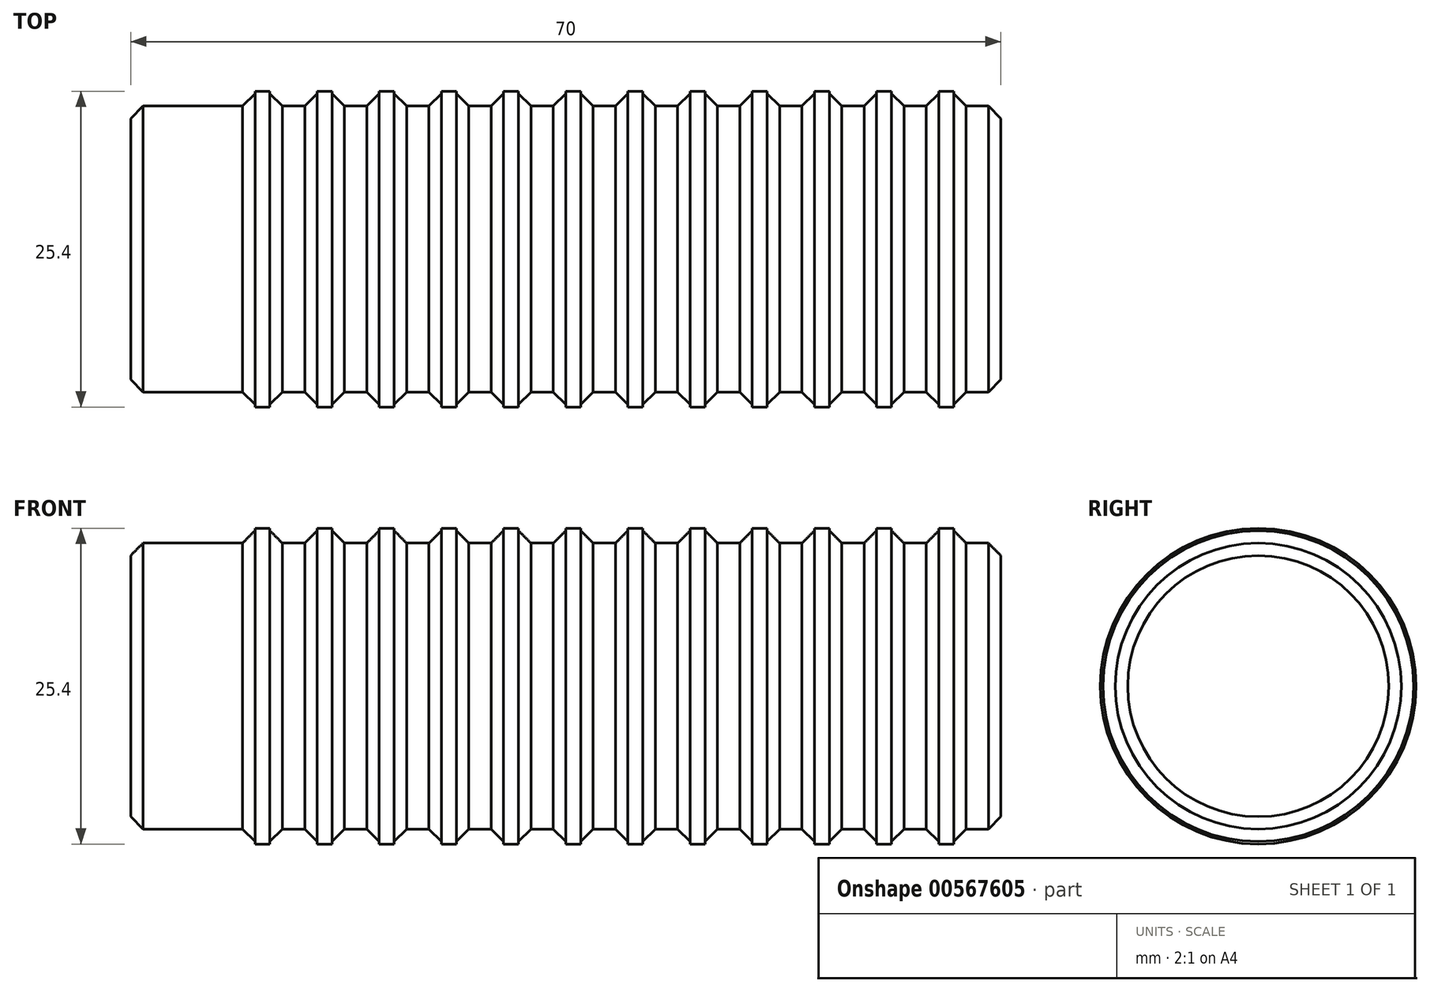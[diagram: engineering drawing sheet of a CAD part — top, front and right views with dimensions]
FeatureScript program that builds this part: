
annotation { "Feature Type Name" : "Feature", "Feature Type Description" : "" }
export const myFeature = defineFeature(function(context is Context, id is Id, definition is map)
    precondition{}
    {
        {
            var Q0;
            Q0=qCreatedBy(makeId("Top.planeOp"),FACE);
            var sketch = newSketch(context, id + "F0", { "sketchPlane" : qUnion([Q0])});
            skLineSegment(sketch, "E0.bottom", {"start": v(-26.21, 0) * mm, "end": v(43.79, 0) * mm});
            skLineSegment(sketch, "E0.top", {"start": v(-26.21, 11.5) * mm, "end": v(43.79, 11.5) * mm});
            skLineSegment(sketch, "E0.left", {"start": v(-26.21, 0) * mm, "end": v(-26.21, 11.5) * mm});
            skLineSegment(sketch, "E0.right", {"start": v(43.79, 0) * mm, "end": v(43.79, 11.5) * mm});
            skLineSegment(sketch, "E1.bottom", {"start": v(-21.21, 11.5) * mm, "end": v(-20.01, 11.5) * mm});
            skLineSegment(sketch, "E1.top", {"start": v(-21.21, 12.7) * mm, "end": v(-20.01, 12.7) * mm});
            skLineSegment(sketch, "E1.left", {"start": v(-21.21, 11.5) * mm, "end": v(-21.21, 12.7) * mm});
            skLineSegment(sketch, "E1.right", {"start": v(-20.01, 11.5) * mm, "end": v(-20.01, 12.7) * mm});
            skLineSegment(sketch, "E2.1.0.0", {"start": v(-15.01, 11.5) * mm, "end": v(-15.01, 12.7) * mm});
            skLineSegment(sketch, "E2.1.0.1", {"start": v(-16.21, 11.5) * mm, "end": v(-16.21, 12.7) * mm});
            skLineSegment(sketch, "E2.1.0.2", {"start": v(-16.21, 12.7) * mm, "end": v(-15.01, 12.7) * mm});
            skLineSegment(sketch, "E2.1.0.3", {"start": v(-16.21, 11.5) * mm, "end": v(-15.01, 11.5) * mm});
            skLineSegment(sketch, "E2.2.0.0", {"start": v(-10.01, 11.5) * mm, "end": v(-10.01, 12.7) * mm});
            skLineSegment(sketch, "E2.2.0.1", {"start": v(-11.21, 11.5) * mm, "end": v(-11.21, 12.7) * mm});
            skLineSegment(sketch, "E2.2.0.2", {"start": v(-11.21, 12.7) * mm, "end": v(-10.01, 12.7) * mm});
            skLineSegment(sketch, "E2.2.0.3", {"start": v(-11.21, 11.5) * mm, "end": v(-10.01, 11.5) * mm});
            skLineSegment(sketch, "E2.3.0.0", {"start": v(-5.01, 11.5) * mm, "end": v(-5.01, 12.7) * mm});
            skLineSegment(sketch, "E2.3.0.1", {"start": v(-6.21, 11.5) * mm, "end": v(-6.21, 12.7) * mm});
            skLineSegment(sketch, "E2.3.0.2", {"start": v(-6.21, 12.7) * mm, "end": v(-5.01, 12.7) * mm});
            skLineSegment(sketch, "E2.3.0.3", {"start": v(-6.21, 11.5) * mm, "end": v(-5.01, 11.5) * mm});
            skLineSegment(sketch, "E2.4.0.0", {"start": v(-0.01, 11.5) * mm, "end": v(-0.01, 12.7) * mm});
            skLineSegment(sketch, "E2.4.0.1", {"start": v(-1.21, 11.5) * mm, "end": v(-1.21, 12.7) * mm});
            skLineSegment(sketch, "E2.4.0.2", {"start": v(-1.21, 12.7) * mm, "end": v(-0.01, 12.7) * mm});
            skLineSegment(sketch, "E2.4.0.3", {"start": v(-1.21, 11.5) * mm, "end": v(-0.01, 11.5) * mm});
            skLineSegment(sketch, "E2.direction1", {"start": v(-21.21, 11.5) * mm, "end": v(-16.21, 11.5) * mm, "construction": true});
            skLineSegment(sketch, "E3.0.5.0", {"start": v(4.99, 11.5) * mm, "end": v(4.99, 12.7) * mm});
            skLineSegment(sketch, "E3.3.5.0", {"start": v(3.79, 11.5) * mm, "end": v(3.79, 12.7) * mm});
            skLineSegment(sketch, "E3.6.5.0", {"start": v(3.79, 12.7) * mm, "end": v(4.99, 12.7) * mm});
            skLineSegment(sketch, "E3.9.5.0", {"start": v(3.79, 11.5) * mm, "end": v(4.99, 11.5) * mm});
            skLineSegment(sketch, "E3.0.6.0", {"start": v(9.99, 11.5) * mm, "end": v(9.99, 12.7) * mm});
            skLineSegment(sketch, "E3.3.6.0", {"start": v(8.79, 11.5) * mm, "end": v(8.79, 12.7) * mm});
            skLineSegment(sketch, "E3.6.6.0", {"start": v(8.79, 12.7) * mm, "end": v(9.99, 12.7) * mm});
            skLineSegment(sketch, "E3.9.6.0", {"start": v(8.79, 11.5) * mm, "end": v(9.99, 11.5) * mm});
            skLineSegment(sketch, "E3.0.7.0", {"start": v(14.99, 11.5) * mm, "end": v(14.99, 12.7) * mm});
            skLineSegment(sketch, "E3.3.7.0", {"start": v(13.79, 11.5) * mm, "end": v(13.79, 12.7) * mm});
            skLineSegment(sketch, "E3.6.7.0", {"start": v(13.79, 12.7) * mm, "end": v(14.99, 12.7) * mm});
            skLineSegment(sketch, "E3.9.7.0", {"start": v(13.79, 11.5) * mm, "end": v(14.99, 11.5) * mm});
            skLineSegment(sketch, "E3.0.8.0", {"start": v(19.99, 11.5) * mm, "end": v(19.99, 12.7) * mm});
            skLineSegment(sketch, "E3.3.8.0", {"start": v(18.79, 11.5) * mm, "end": v(18.79, 12.7) * mm});
            skLineSegment(sketch, "E3.6.8.0", {"start": v(18.79, 12.7) * mm, "end": v(19.99, 12.7) * mm});
            skLineSegment(sketch, "E3.9.8.0", {"start": v(18.79, 11.5) * mm, "end": v(19.99, 11.5) * mm});
            skLineSegment(sketch, "E4.0.9.0", {"start": v(24.99, 11.5) * mm, "end": v(24.99, 12.7) * mm});
            skLineSegment(sketch, "E4.3.9.0", {"start": v(23.79, 11.5) * mm, "end": v(23.79, 12.7) * mm});
            skLineSegment(sketch, "E4.6.9.0", {"start": v(23.79, 12.7) * mm, "end": v(24.99, 12.7) * mm});
            skLineSegment(sketch, "E4.9.9.0", {"start": v(23.79, 11.5) * mm, "end": v(24.99, 11.5) * mm});
            skLineSegment(sketch, "E4.0.10.0", {"start": v(29.99, 11.5) * mm, "end": v(29.99, 12.7) * mm});
            skLineSegment(sketch, "E4.3.10.0", {"start": v(28.79, 11.5) * mm, "end": v(28.79, 12.7) * mm});
            skLineSegment(sketch, "E4.6.10.0", {"start": v(28.79, 12.7) * mm, "end": v(29.99, 12.7) * mm});
            skLineSegment(sketch, "E4.9.10.0", {"start": v(28.79, 11.5) * mm, "end": v(29.99, 11.5) * mm});
            skLineSegment(sketch, "E4.0.11.0", {"start": v(34.99, 11.5) * mm, "end": v(34.99, 12.7) * mm});
            skLineSegment(sketch, "E4.3.11.0", {"start": v(33.79, 11.5) * mm, "end": v(33.79, 12.7) * mm});
            skLineSegment(sketch, "E4.6.11.0", {"start": v(33.79, 12.7) * mm, "end": v(34.99, 12.7) * mm});
            skLineSegment(sketch, "E4.9.11.0", {"start": v(33.79, 11.5) * mm, "end": v(34.99, 11.5) * mm});
            skLineSegment(sketch, "E4.0.12.0", {"start": v(39.99, 11.5) * mm, "end": v(39.99, 12.7) * mm});
            skLineSegment(sketch, "E4.3.12.0", {"start": v(38.79, 11.5) * mm, "end": v(38.79, 12.7) * mm});
            skLineSegment(sketch, "E4.6.12.0", {"start": v(38.79, 12.7) * mm, "end": v(39.99, 12.7) * mm});
            skLineSegment(sketch, "E4.9.12.0", {"start": v(38.79, 11.5) * mm, "end": v(39.99, 11.5) * mm});
            skSolve(sketch);
        }
        {
            var Q0;
            Q0=makeQuery(id+"F0.imprint","IMPRINT",FACE,{"disambiguationData":[TD([[makeQuery(id+"F0.imprint","IMPRINT",EDGE,{"derivedFrom":sQuery(id+"F0.wireOp",EDGE,"E0.bottom")}),1.0]])]});
            var Q1;
            Q1=makeQuery(id+"F0.imprint","IMPRINT",FACE,{"disambiguationData":[TD([[makeQuery(id+"F0.imprint","IMPRINT",EDGE,{"derivedFrom":sQuery(id+"F0.wireOp",EDGE,"E3.0.8.0")}),1.0]])]});
            var Q2;
            Q2=makeQuery(id+"F0.imprint","IMPRINT",FACE,{"disambiguationData":[TD([[makeQuery(id+"F0.imprint","IMPRINT",EDGE,{"derivedFrom":sQuery(id+"F0.wireOp",EDGE,"E3.0.7.0")}),1.0]])]});
            var Q3;
            Q3=makeQuery(id+"F0.imprint","IMPRINT",FACE,{"disambiguationData":[TD([[makeQuery(id+"F0.imprint","IMPRINT",EDGE,{"derivedFrom":sQuery(id+"F0.wireOp",EDGE,"E3.0.6.0")}),1.0]])]});
            var Q4;
            Q4=makeQuery(id+"F0.imprint","IMPRINT",FACE,{"disambiguationData":[TD([[makeQuery(id+"F0.imprint","IMPRINT",EDGE,{"derivedFrom":sQuery(id+"F0.wireOp",EDGE,"E3.0.5.0")}),1.0]])]});
            var Q5;
            Q5=makeQuery(id+"F0.imprint","IMPRINT",FACE,{"disambiguationData":[TD([[makeQuery(id+"F0.imprint","IMPRINT",EDGE,{"derivedFrom":sQuery(id+"F0.wireOp",EDGE,"E2.4.0.0")}),1.0]])]});
            var Q6;
            Q6=makeQuery(id+"F0.imprint","IMPRINT",FACE,{"disambiguationData":[TD([[makeQuery(id+"F0.imprint","IMPRINT",EDGE,{"derivedFrom":sQuery(id+"F0.wireOp",EDGE,"E2.3.0.0")}),1.0]])]});
            var Q7;
            Q7=makeQuery(id+"F0.imprint","IMPRINT",FACE,{"disambiguationData":[TD([[makeQuery(id+"F0.imprint","IMPRINT",EDGE,{"derivedFrom":sQuery(id+"F0.wireOp",EDGE,"E2.2.0.0")}),1.0]])]});
            var Q8;
            Q8=makeQuery(id+"F0.imprint","IMPRINT",FACE,{"disambiguationData":[TD([[makeQuery(id+"F0.imprint","IMPRINT",EDGE,{"derivedFrom":sQuery(id+"F0.wireOp",EDGE,"E2.1.0.0")}),1.0]])]});
            var Q9;
            Q9=makeQuery(id+"F0.imprint","IMPRINT",FACE,{"disambiguationData":[TD([[makeQuery(id+"F0.imprint","IMPRINT",EDGE,{"derivedFrom":sQuery(id+"F0.wireOp",EDGE,"E1.bottom")}),1.0]])]});
            var Q10;
            Q10=makeQuery(id+"F0.imprint","IMPRINT",FACE,{"disambiguationData":[TD([[makeQuery(id+"F0.imprint","IMPRINT",EDGE,{"derivedFrom":sQuery(id+"F0.wireOp",EDGE,"E4.0.9.0")}),1.0]])]});
            var Q11;
            Q11=makeQuery(id+"F0.imprint","IMPRINT",FACE,{"disambiguationData":[TD([[makeQuery(id+"F0.imprint","IMPRINT",EDGE,{"derivedFrom":sQuery(id+"F0.wireOp",EDGE,"E4.0.10.0")}),1.0]])]});
            var Q12;
            Q12=makeQuery(id+"F0.imprint","IMPRINT",FACE,{"disambiguationData":[TD([[makeQuery(id+"F0.imprint","IMPRINT",EDGE,{"derivedFrom":sQuery(id+"F0.wireOp",EDGE,"E4.0.11.0")}),1.0]])]});
            var Q13;
            Q13=makeQuery(id+"F0.imprint","IMPRINT",FACE,{"disambiguationData":[TD([[makeQuery(id+"F0.imprint","IMPRINT",EDGE,{"derivedFrom":sQuery(id+"F0.wireOp",EDGE,"E4.0.12.0")}),1.0]])]});
            var Q14;
            Q14=sQuery(id+"F0.wireOp",EDGE,"E0.bottom");
            revolve(context, id + "F1", {"entities" : qUnion([Q0, Q1, Q2, Q3, Q4, Q5, Q6, Q7, Q8, Q9, Q10, Q11, Q12, Q13]), "axis" : qUnion([Q14]), "revolveType" : RevolveType.FULL});
        }
        {
            var Q0;
            Q0=makeQuery(id+"F1.opRevolve","SWEPT_EDGE",EDGE,{"disambiguationData":[OSD([sQuery(id+"F0.wireOp",EDGE,"E0.top"),sQuery(id+"F0.wireOp",EDGE,"E1.bottom"),sQuery(id+"F0.wireOp",EDGE,"E1.left")])]});
            var Q1;
            Q1=makeQuery(id+"F1.opRevolve","SWEPT_EDGE",EDGE,{"disambiguationData":[OSD([sQuery(id+"F0.wireOp",EDGE,"E0.top"),sQuery(id+"F0.wireOp",EDGE,"E2.1.0.1"),sQuery(id+"F0.wireOp",EDGE,"E2.1.0.3")])]});
            var Q2;
            Q2=makeQuery(id+"F1.opRevolve","SWEPT_EDGE",EDGE,{"disambiguationData":[OSD([sQuery(id+"F0.wireOp",EDGE,"E0.top"),sQuery(id+"F0.wireOp",EDGE,"E2.2.0.1"),sQuery(id+"F0.wireOp",EDGE,"E2.2.0.3")])]});
            var Q3;
            Q3=makeQuery(id+"F1.opRevolve","SWEPT_EDGE",EDGE,{"disambiguationData":[OSD([sQuery(id+"F0.wireOp",EDGE,"E0.top"),sQuery(id+"F0.wireOp",EDGE,"E2.3.0.1"),sQuery(id+"F0.wireOp",EDGE,"E2.3.0.3")])]});
            var Q4;
            Q4=makeQuery(id+"F1.opRevolve","SWEPT_EDGE",EDGE,{"disambiguationData":[OSD([sQuery(id+"F0.wireOp",EDGE,"E0.top"),sQuery(id+"F0.wireOp",EDGE,"E3.0.8.0"),sQuery(id+"F0.wireOp",EDGE,"E3.9.8.0")])]});
            var Q5;
            Q5=makeQuery(id+"F1.opRevolve","SWEPT_EDGE",EDGE,{"disambiguationData":[OSD([sQuery(id+"F0.wireOp",EDGE,"E0.top"),sQuery(id+"F0.wireOp",EDGE,"E3.0.7.0"),sQuery(id+"F0.wireOp",EDGE,"E3.9.7.0")])]});
            var Q6;
            Q6=makeQuery(id+"F1.opRevolve","SWEPT_EDGE",EDGE,{"disambiguationData":[OSD([sQuery(id+"F0.wireOp",EDGE,"E0.top"),sQuery(id+"F0.wireOp",EDGE,"E3.0.6.0"),sQuery(id+"F0.wireOp",EDGE,"E3.9.6.0")])]});
            var Q7;
            Q7=makeQuery(id+"F1.opRevolve","SWEPT_EDGE",EDGE,{"disambiguationData":[OSD([sQuery(id+"F0.wireOp",EDGE,"E0.top"),sQuery(id+"F0.wireOp",EDGE,"E3.0.5.0"),sQuery(id+"F0.wireOp",EDGE,"E3.9.5.0")])]});
            var Q8;
            Q8=makeQuery(id+"F1.opRevolve","SWEPT_EDGE",EDGE,{"disambiguationData":[OSD([sQuery(id+"F0.wireOp",EDGE,"E0.top"),sQuery(id+"F0.wireOp",EDGE,"E2.4.0.1"),sQuery(id+"F0.wireOp",EDGE,"E2.4.0.3")])]});
            var Q9;
            Q9=makeQuery(id+"F1.opRevolve","SWEPT_EDGE",EDGE,{"disambiguationData":[OSD([sQuery(id+"F0.wireOp",EDGE,"E0.top"),sQuery(id+"F0.wireOp",EDGE,"E2.4.0.0"),sQuery(id+"F0.wireOp",EDGE,"E2.4.0.3")])]});
            var Q10;
            Q10=makeQuery(id+"F1.opRevolve","SWEPT_EDGE",EDGE,{"disambiguationData":[OSD([sQuery(id+"F0.wireOp",EDGE,"E0.top"),sQuery(id+"F0.wireOp",EDGE,"E1.bottom"),sQuery(id+"F0.wireOp",EDGE,"E1.right")])]});
            var Q11;
            Q11=makeQuery(id+"F1.opRevolve","SWEPT_EDGE",EDGE,{"disambiguationData":[OSD([sQuery(id+"F0.wireOp",EDGE,"E0.top"),sQuery(id+"F0.wireOp",EDGE,"E2.1.0.0"),sQuery(id+"F0.wireOp",EDGE,"E2.1.0.3")])]});
            var Q12;
            Q12=makeQuery(id+"F1.opRevolve","SWEPT_EDGE",EDGE,{"disambiguationData":[OSD([sQuery(id+"F0.wireOp",EDGE,"E0.top"),sQuery(id+"F0.wireOp",EDGE,"E2.2.0.0"),sQuery(id+"F0.wireOp",EDGE,"E2.2.0.3")])]});
            var Q13;
            Q13=makeQuery(id+"F1.opRevolve","SWEPT_EDGE",EDGE,{"disambiguationData":[OSD([sQuery(id+"F0.wireOp",EDGE,"E0.top"),sQuery(id+"F0.wireOp",EDGE,"E2.3.0.0"),sQuery(id+"F0.wireOp",EDGE,"E2.3.0.3")])]});
            var Q14;
            Q14=makeQuery(id+"F1.opRevolve","SWEPT_EDGE",EDGE,{"disambiguationData":[OSD([sQuery(id+"F0.wireOp",EDGE,"E0.top"),sQuery(id+"F0.wireOp",EDGE,"E3.3.5.0"),sQuery(id+"F0.wireOp",EDGE,"E3.9.5.0")])]});
            var Q15;
            Q15=makeQuery(id+"F1.opRevolve","SWEPT_EDGE",EDGE,{"disambiguationData":[OSD([sQuery(id+"F0.wireOp",EDGE,"E0.top"),sQuery(id+"F0.wireOp",EDGE,"E3.3.6.0"),sQuery(id+"F0.wireOp",EDGE,"E3.9.6.0")])]});
            var Q16;
            Q16=makeQuery(id+"F1.opRevolve","SWEPT_EDGE",EDGE,{"disambiguationData":[OSD([sQuery(id+"F0.wireOp",EDGE,"E0.top"),sQuery(id+"F0.wireOp",EDGE,"E3.3.7.0"),sQuery(id+"F0.wireOp",EDGE,"E3.9.7.0")])]});
            var Q17;
            Q17=makeQuery(id+"F1.opRevolve","SWEPT_EDGE",EDGE,{"disambiguationData":[OSD([sQuery(id+"F0.wireOp",EDGE,"E0.top"),sQuery(id+"F0.wireOp",EDGE,"E3.3.8.0"),sQuery(id+"F0.wireOp",EDGE,"E3.9.8.0")])]});
            var Q18;
            Q18=makeQuery(id+"F1.opRevolve","SWEPT_EDGE",EDGE,{"disambiguationData":[OSD([sQuery(id+"F0.wireOp",EDGE,"E0.top"),sQuery(id+"F0.wireOp",EDGE,"E4.3.9.0"),sQuery(id+"F0.wireOp",EDGE,"E4.9.9.0")])]});
            var Q19;
            Q19=makeQuery(id+"F1.opRevolve","SWEPT_EDGE",EDGE,{"disambiguationData":[OSD([sQuery(id+"F0.wireOp",EDGE,"E0.top"),sQuery(id+"F0.wireOp",EDGE,"E4.0.9.0"),sQuery(id+"F0.wireOp",EDGE,"E4.9.9.0")])]});
            var Q20;
            Q20=makeQuery(id+"F1.opRevolve","SWEPT_EDGE",EDGE,{"disambiguationData":[OSD([sQuery(id+"F0.wireOp",EDGE,"E0.top"),sQuery(id+"F0.wireOp",EDGE,"E4.3.10.0"),sQuery(id+"F0.wireOp",EDGE,"E4.9.10.0")])]});
            var Q21;
            Q21=makeQuery(id+"F1.opRevolve","SWEPT_EDGE",EDGE,{"disambiguationData":[OSD([sQuery(id+"F0.wireOp",EDGE,"E0.top"),sQuery(id+"F0.wireOp",EDGE,"E4.0.10.0"),sQuery(id+"F0.wireOp",EDGE,"E4.9.10.0")])]});
            var Q22;
            Q22=makeQuery(id+"F1.opRevolve","SWEPT_EDGE",EDGE,{"disambiguationData":[OSD([sQuery(id+"F0.wireOp",EDGE,"E0.top"),sQuery(id+"F0.wireOp",EDGE,"E4.3.11.0"),sQuery(id+"F0.wireOp",EDGE,"E4.9.11.0")])]});
            var Q23;
            Q23=makeQuery(id+"F1.opRevolve","SWEPT_EDGE",EDGE,{"disambiguationData":[OSD([sQuery(id+"F0.wireOp",EDGE,"E0.top"),sQuery(id+"F0.wireOp",EDGE,"E4.0.11.0"),sQuery(id+"F0.wireOp",EDGE,"E4.9.11.0")])]});
            var Q24;
            Q24=makeQuery(id+"F1.opRevolve","SWEPT_EDGE",EDGE,{"disambiguationData":[OSD([sQuery(id+"F0.wireOp",EDGE,"E0.top"),sQuery(id+"F0.wireOp",EDGE,"E4.3.12.0"),sQuery(id+"F0.wireOp",EDGE,"E4.9.12.0")])]});
            var Q25;
            Q25=makeQuery(id+"F1.opRevolve","SWEPT_EDGE",EDGE,{"disambiguationData":[OSD([sQuery(id+"F0.wireOp",EDGE,"E0.top"),sQuery(id+"F0.wireOp",EDGE,"E4.0.12.0"),sQuery(id+"F0.wireOp",EDGE,"E4.9.12.0")])]});
            chamfer(context, id + "F2", {"entities" : qUnion([Q0, Q1, Q2, Q3, Q4, Q5, Q6, Q7, Q8, Q9, Q10, Q11, Q12, Q13, Q14, Q15, Q16, Q17, Q18, Q19, Q20, Q21, Q22, Q23, Q24, Q25]), "width" : 1 * mm, "tangentPropagation" : true});
        }
    });
